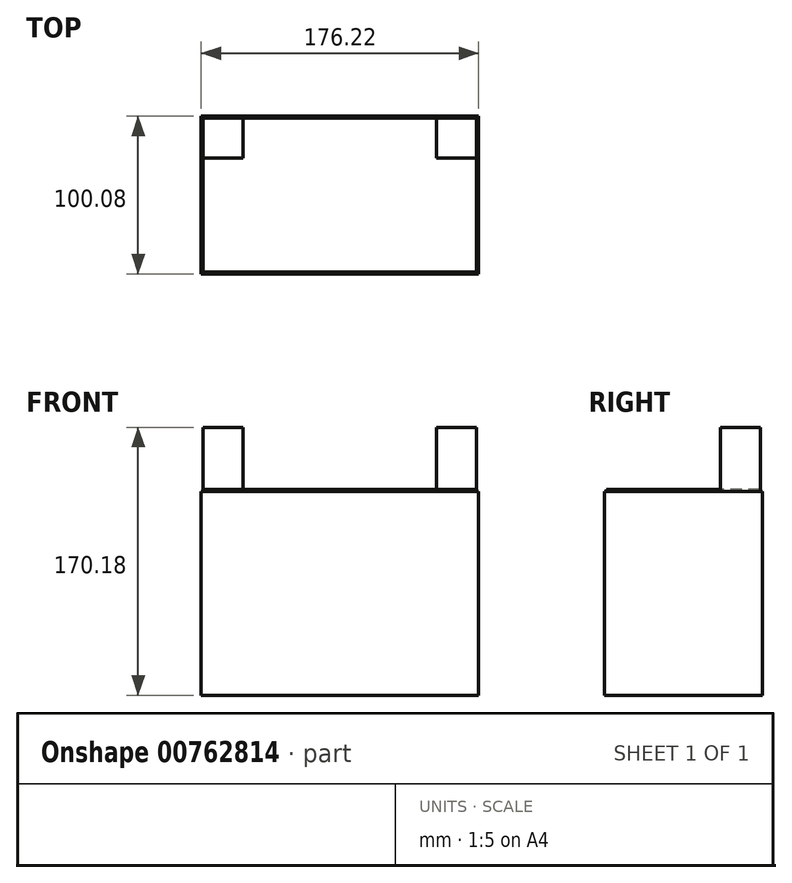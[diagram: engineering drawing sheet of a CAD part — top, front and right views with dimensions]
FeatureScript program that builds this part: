
annotation { "Feature Type Name" : "Feature", "Feature Type Description" : "" }
export const myFeature = defineFeature(function(context is Context, id is Id, definition is map)
    precondition{}
    {
        {
            var Q0;
            Q0=qCreatedBy(makeId("Top.planeOp"),FACE);
            var sketch = newSketch(context, id + "F0", { "sketchPlane" : qUnion([Q0])});
            skLineSegment(sketch, "E0.bottom", {"start": v(-88.1, 50.04) * mm, "end": v(88.1, 50.04) * mm});
            skLineSegment(sketch, "E0.top", {"start": v(-88.1, -50.04) * mm, "end": v(88.1, -50.04) * mm});
            skLineSegment(sketch, "E0.left", {"start": v(-88.1, 50.04) * mm, "end": v(-88.1, -50.04) * mm});
            skLineSegment(sketch, "E0.right", {"start": v(88.1, 50.04) * mm, "end": v(88.1, -50.04) * mm});
            skPoint(sketch, "E0.middle", {"position": v(0, 0) * mm});
            skSolve(sketch);
        }
        {
            var Q0;
            Q0=makeQuery(id+"F0.imprint","IMPRINT",FACE,{"disambiguationData":[TD([[makeQuery(id+"F0.imprint","IMPRINT",EDGE,{"derivedFrom":sQuery(id+"F0.wireOp",EDGE,"E0.bottom")}),-1.0]])]});
            extrude(context, id + "F1", {"entities" : qUnion([Q0]), "endBound" : BoundingType.SYMMETRIC, "depth" : 129.54 * mm, "offsetDistance" : 25.4 * mm});
        }
        {
            var Q0;
            Q0=makeQuery(id+"F1.opExtrude","CAP_FACE",FACE,{"disambiguationData":[OSD([sQuery(id+"F0.wireOp",EDGE,"E0.bottom"),sQuery(id+"F0.wireOp",EDGE,"E0.top"),sQuery(id+"F0.wireOp",EDGE,"E0.left"),sQuery(id+"F0.wireOp",EDGE,"E0.right")])],"isStart":false});
            var sketch = newSketch(context, id + "F2", { "sketchPlane" : qUnion([Q0])});
            skLineSegment(sketch, "E1.bottom", {"start": v(-86.84, 48.77) * mm, "end": v(86.84, 48.77) * mm});
            skLineSegment(sketch, "E1.top", {"start": v(-86.84, -48.77) * mm, "end": v(86.84, -48.77) * mm});
            skLineSegment(sketch, "E1.left", {"start": v(-86.84, 48.77) * mm, "end": v(-86.84, -48.77) * mm});
            skLineSegment(sketch, "E1.right", {"start": v(86.84, 48.77) * mm, "end": v(86.84, -48.77) * mm});
            skPoint(sketch, "E1.middle", {"position": v(0, 0) * mm});
            skSolve(sketch);
        }
        {
            var Q0;
            Q0=makeQuery(id+"F2.imprint","IMPRINT",FACE,{"disambiguationData":[TD([[makeQuery(id+"F2.imprint","IMPRINT",EDGE,{"derivedFrom":sQuery(id+"F2.wireOp",EDGE,"E1.bottom")}),-1.0]])]});
            extrude(context, id + "F3", {"entities" : qUnion([Q0]), "operationType" : NewBodyOperationType.ADD, "depth" : 1.27 * mm, "offsetDistance" : 25.4 * mm});
        }
        {
            var Q0;
            Q0=makeQuery(id+"F3.opExtrude","CAP_FACE",FACE,{"disambiguationData":[OSD([sQuery(id+"F2.wireOp",EDGE,"E1.bottom"),sQuery(id+"F2.wireOp",EDGE,"E1.top"),sQuery(id+"F2.wireOp",EDGE,"E1.left"),sQuery(id+"F2.wireOp",EDGE,"E1.right")])],"isStart":false});
            var sketch = newSketch(context, id + "F4", { "sketchPlane" : qUnion([Q0])});
            skLineSegment(sketch, "E2.bottom", {"start": v(-86.84, 48.77) * mm, "end": v(86.84, 48.77) * mm});
            skLineSegment(sketch, "E2.top", {"start": v(-86.84, -48.77) * mm, "end": v(86.84, -48.77) * mm});
            skLineSegment(sketch, "E2.left", {"start": v(-86.84, 48.77) * mm, "end": v(-86.84, -48.77) * mm});
            skLineSegment(sketch, "E2.right", {"start": v(86.84, 48.77) * mm, "end": v(86.84, -48.77) * mm});
            skPoint(sketch, "E2.middle", {"position": v(0, 0) * mm});
            skLineSegment(sketch, "E3.bottom", {"start": v(-86.84, 48.77) * mm, "end": v(-61.44, 48.77) * mm});
            skLineSegment(sketch, "E3.top", {"start": v(-86.84, 23.37) * mm, "end": v(-61.44, 23.37) * mm});
            skLineSegment(sketch, "E3.left", {"start": v(-86.84, 48.77) * mm, "end": v(-86.84, 23.37) * mm});
            skLineSegment(sketch, "E3.right", {"start": v(-61.44, 48.77) * mm, "end": v(-61.44, 23.37) * mm});
            skLineSegment(sketch, "E4.bottom", {"start": v(86.84, 48.77) * mm, "end": v(61.44, 48.77) * mm});
            skLineSegment(sketch, "E4.top", {"start": v(86.84, 23.37) * mm, "end": v(61.44, 23.37) * mm});
            skLineSegment(sketch, "E4.left", {"start": v(86.84, 48.77) * mm, "end": v(86.84, 23.37) * mm});
            skLineSegment(sketch, "E4.right", {"start": v(61.44, 48.77) * mm, "end": v(61.44, 23.37) * mm});
            skSolve(sketch);
        }
        {
            var Q0;
            Q0=makeQuery(id+"F4.imprint","IMPRINT",FACE,{"disambiguationData":[TD([[makeQuery(id+"F4.imprint","IMPRINT",EDGE,{"derivedFrom":sQuery(id+"F4.wireOp",EDGE,"E2.bottom")}),-1.0]])]});
            extrude(context, id + "F5", {"entities" : qUnion([Q0]), "operationType" : NewBodyOperationType.ADD, "depth" : 39.37 * mm, "offsetDistance" : 25.4 * mm});
        }
    });
